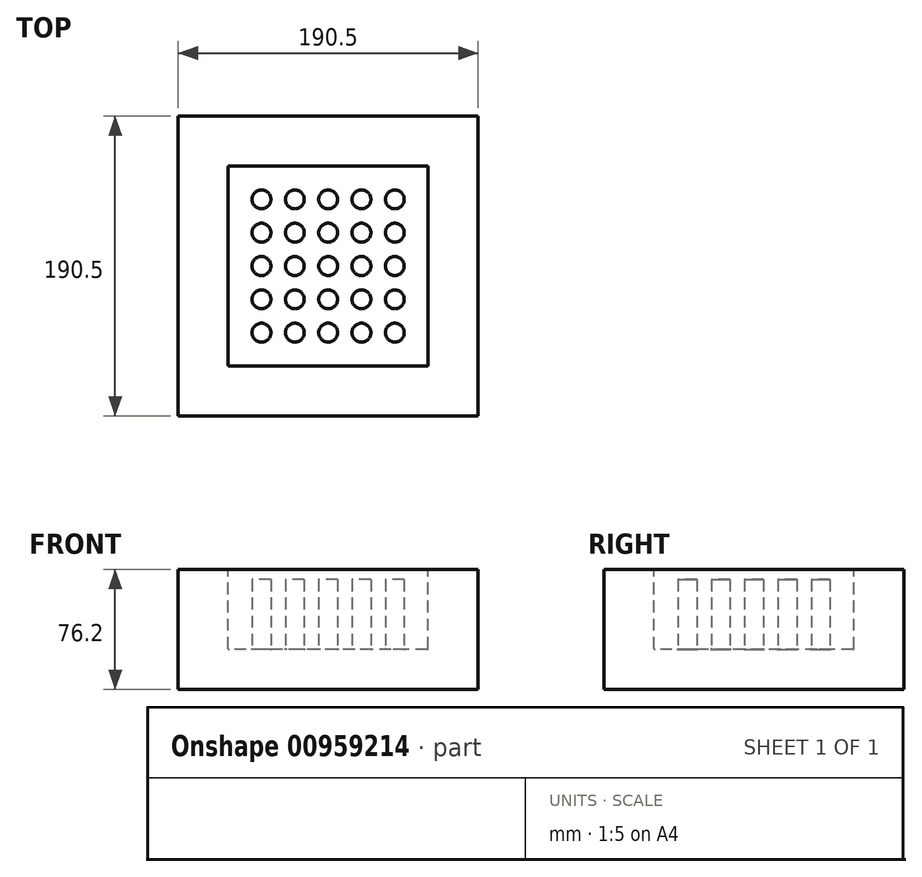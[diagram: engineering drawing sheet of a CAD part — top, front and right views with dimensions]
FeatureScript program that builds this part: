
annotation { "Feature Type Name" : "Feature", "Feature Type Description" : "" }
export const myFeature = defineFeature(function(context is Context, id is Id, definition is map)
    precondition{}
    {
        {
            var Q0;
            Q0=qCreatedBy(makeId("Top.planeOp"),FACE);
            var sketch = newSketch(context, id + "F0", { "sketchPlane" : qUnion([Q0])});
            skLineSegment(sketch, "E0.bottom", {"start": v(95.25, 95.25) * mm, "end": v(-95.25, 95.25) * mm});
            skLineSegment(sketch, "E0.top", {"start": v(95.25, -95.25) * mm, "end": v(-95.25, -95.25) * mm});
            skLineSegment(sketch, "E0.left", {"start": v(95.25, 95.25) * mm, "end": v(95.25, -95.25) * mm});
            skLineSegment(sketch, "E0.right", {"start": v(-95.25, 95.25) * mm, "end": v(-95.25, -95.25) * mm});
            skPoint(sketch, "E0.middle", {"position": v(0, 0) * mm});
            skSolve(sketch);
        }
        {
            var Q0;
            Q0 = qSketchRegion(id + "F0", true);
            extrude(context, id + "F1", {"entities" : qUnion([Q0]), "depth" : 76.2 * mm, "offsetDistance" : 25.4 * mm});
        }
        {
            var Q0;
            Q0=makeQuery(id+"F1.opExtrude","CAP_FACE",FACE,{"disambiguationData":[OSD([sQuery(id+"F0.wireOp",EDGE,"E0.bottom"),sQuery(id+"F0.wireOp",EDGE,"E0.top"),sQuery(id+"F0.wireOp",EDGE,"E0.left"),sQuery(id+"F0.wireOp",EDGE,"E0.right")])],"isStart":false});
            var sketch = newSketch(context, id + "F2", { "sketchPlane" : qUnion([Q0])});
            skLineSegment(sketch, "E1.bottom", {"start": v(63.5, 63.5) * mm, "end": v(-63.5, 63.5) * mm});
            skLineSegment(sketch, "E1.top", {"start": v(63.5, -63.5) * mm, "end": v(-63.5, -63.5) * mm});
            skLineSegment(sketch, "E1.left", {"start": v(63.5, 63.5) * mm, "end": v(63.5, -63.5) * mm});
            skLineSegment(sketch, "E1.right", {"start": v(-63.5, 63.5) * mm, "end": v(-63.5, -63.5) * mm});
            skPoint(sketch, "E1.middle", {"position": v(0, 0) * mm});
            skSolve(sketch);
        }
        {
            var Q0;
            Q0 = qSketchRegion(id + "F2", true);
            extrude(context, id + "F3", {"entities" : qUnion([Q0]), "operationType" : NewBodyOperationType.REMOVE, "oppositeDirection" : true, "depth" : 50.8 * mm, "offsetDistance" : 25.4 * mm});
        }
        {
            var Q0;
            Q0=makeQuery(id+"F3.boolean.opBoolean","COPY",FACE,{"derivedFrom":makeQuery(id+"F3.opExtrude","CAP_FACE",FACE,{"disambiguationData":[OSD([sQuery(id+"F2.wireOp",EDGE,"E1.bottom"),sQuery(id+"F2.wireOp",EDGE,"E1.top"),sQuery(id+"F2.wireOp",EDGE,"E1.left"),sQuery(id+"F2.wireOp",EDGE,"E1.right")])],"isStart":false})});
            var sketch = newSketch(context, id + "F4", { "sketchPlane" : qUnion([Q0])});
            skLineSegment(sketch, "E2", {"start": v(-63.5, 63.5) * mm, "end": v(-63.5, -63.5) * mm, "construction": true});
            skLineSegment(sketch, "E3.1.0.0", {"start": v(-42.33, 63.5) * mm, "end": v(-42.33, -63.5) * mm, "construction": true});
            skLineSegment(sketch, "E3.2.0.0", {"start": v(-21.17, 63.5) * mm, "end": v(-21.17, -63.5) * mm, "construction": true});
            skLineSegment(sketch, "E3.3.0.0", {"start": v(0, 63.5) * mm, "end": v(0, -63.5) * mm, "construction": true});
            skLineSegment(sketch, "E3.4.0.0", {"start": v(21.17, 63.5) * mm, "end": v(21.17, -63.5) * mm, "construction": true});
            skLineSegment(sketch, "E3.5.0.0", {"start": v(42.33, 63.5) * mm, "end": v(42.33, -63.5) * mm, "construction": true});
            skLineSegment(sketch, "E3.direction1", {"start": v(-63.5, -63.5) * mm, "end": v(-42.33, -63.5) * mm, "construction": true});
            skLineSegment(sketch, "E4", {"start": v(-63.5, -63.5) * mm, "end": v(63.5, -63.5) * mm, "construction": true});
            skLineSegment(sketch, "E5.0.1.0", {"start": v(-63.5, -42.33) * mm, "end": v(63.5, -42.33) * mm, "construction": true});
            skLineSegment(sketch, "E5.0.2.0", {"start": v(-63.5, -21.17) * mm, "end": v(63.5, -21.17) * mm, "construction": true});
            skLineSegment(sketch, "E5.0.3.0", {"start": v(-63.5, 0) * mm, "end": v(63.5, 0) * mm, "construction": true});
            skLineSegment(sketch, "E5.0.4.0", {"start": v(-63.5, 21.17) * mm, "end": v(63.5, 21.17) * mm, "construction": true});
            skLineSegment(sketch, "E5.0.5.0", {"start": v(-63.5, 42.33) * mm, "end": v(63.5, 42.33) * mm, "construction": true});
            skLineSegment(sketch, "E5.direction1", {"start": v(-63.5, -63.5) * mm, "end": v(-38.5, -63.5) * mm, "construction": true});
            skLineSegment(sketch, "E5.direction2", {"start": v(-63.5, -63.5) * mm, "end": v(-63.5, -42.33) * mm, "construction": true});
            skCircle(sketch, "E6", {"center": v(-42.33, -42.33) * mm, "radius": 6 * mm});
            skCircle(sketch, "E7.0.1.0", {"center": v(-42.33, -21.17) * mm, "radius": 6 * mm});
            skCircle(sketch, "E7.0.2.0", {"center": v(-42.33, 0) * mm, "radius": 6 * mm});
            skCircle(sketch, "E7.0.3.0", {"center": v(-42.33, 21.17) * mm, "radius": 6 * mm});
            skCircle(sketch, "E7.0.4.0", {"center": v(-42.33, 42.33) * mm, "radius": 6 * mm});
            skCircle(sketch, "E7.1.0.0", {"center": v(-21.17, -42.33) * mm, "radius": 6 * mm});
            skCircle(sketch, "E7.1.1.0", {"center": v(-21.17, -21.17) * mm, "radius": 6 * mm});
            skCircle(sketch, "E7.1.2.0", {"center": v(-21.17, 0) * mm, "radius": 6 * mm});
            skCircle(sketch, "E7.1.3.0", {"center": v(-21.17, 21.17) * mm, "radius": 6 * mm});
            skCircle(sketch, "E7.1.4.0", {"center": v(-21.17, 42.33) * mm, "radius": 6 * mm});
            skCircle(sketch, "E7.2.0.0", {"center": v(0, -42.33) * mm, "radius": 6 * mm});
            skCircle(sketch, "E7.2.1.0", {"center": v(0, -21.17) * mm, "radius": 6 * mm});
            skCircle(sketch, "E7.2.2.0", {"center": v(0, 0) * mm, "radius": 6 * mm});
            skCircle(sketch, "E7.2.3.0", {"center": v(0, 21.17) * mm, "radius": 6 * mm});
            skCircle(sketch, "E7.2.4.0", {"center": v(0, 42.33) * mm, "radius": 6 * mm});
            skCircle(sketch, "E7.3.0.0", {"center": v(21.17, -42.33) * mm, "radius": 6 * mm});
            skCircle(sketch, "E7.3.1.0", {"center": v(21.17, -21.17) * mm, "radius": 6 * mm});
            skCircle(sketch, "E7.3.2.0", {"center": v(21.17, 0) * mm, "radius": 6 * mm});
            skCircle(sketch, "E7.3.3.0", {"center": v(21.17, 21.17) * mm, "radius": 6 * mm});
            skCircle(sketch, "E7.3.4.0", {"center": v(21.17, 42.33) * mm, "radius": 6 * mm});
            skCircle(sketch, "E7.4.0.0", {"center": v(42.33, -42.33) * mm, "radius": 6 * mm});
            skCircle(sketch, "E7.4.1.0", {"center": v(42.33, -21.17) * mm, "radius": 6 * mm});
            skCircle(sketch, "E7.4.2.0", {"center": v(42.33, 0) * mm, "radius": 6 * mm});
            skCircle(sketch, "E7.4.3.0", {"center": v(42.33, 21.17) * mm, "radius": 6 * mm});
            skCircle(sketch, "E7.4.4.0", {"center": v(42.33, 42.33) * mm, "radius": 6 * mm});
            skLineSegment(sketch, "E7.direction1", {"start": v(-42.33, -42.33) * mm, "end": v(-21.17, -42.33) * mm, "construction": true});
            skLineSegment(sketch, "E7.direction2", {"start": v(-42.33, -42.33) * mm, "end": v(-42.33, -21.17) * mm, "construction": true});
            skSolve(sketch);
        }
        {
            var Q0;
            Q0 = qSketchRegion(id + "F4", true);
            extrude(context, id + "F5", {"entities" : qUnion([Q0]), "operationType" : NewBodyOperationType.ADD, "depth" : 44.45 * mm, "offsetDistance" : 25 * mm});
        }
        {
            var Q0;
            Q0=makeQuery(id+"F3.boolean.opBoolean","COPY",FACE,{"derivedFrom":makeQuery(id+"F3.opExtrude","CAP_FACE",FACE,{"disambiguationData":[OSD([sQuery(id+"F2.wireOp",EDGE,"E1.bottom"),sQuery(id+"F2.wireOp",EDGE,"E1.top"),sQuery(id+"F2.wireOp",EDGE,"E1.left"),sQuery(id+"F2.wireOp",EDGE,"E1.right")])],"isStart":false})});
            var Q1;
            Q1=makeQuery(id+"F3.boolean.opBoolean","COPY",EDGE,{"derivedFrom":makeQuery(id+"F3.opExtrude","SWEPT_EDGE",EDGE,{"disambiguationData":[OSD([sQuery(id+"F2.wireOp",EDGE,"E1.bottom"),sQuery(id+"F2.wireOp",EDGE,"E1.left")])]})});
            var Q2;
            Q2=makeQuery(id+"F3.boolean.opBoolean","COPY",EDGE,{"derivedFrom":makeQuery(id+"F3.opExtrude","SWEPT_EDGE",EDGE,{"disambiguationData":[OSD([sQuery(id+"F2.wireOp",EDGE,"E1.bottom"),sQuery(id+"F2.wireOp",EDGE,"E1.right")])]})});
            var Q3;
            Q3=makeQuery(id+"F3.boolean.opBoolean","COPY",EDGE,{"derivedFrom":makeQuery(id+"F3.opExtrude","SWEPT_EDGE",EDGE,{"disambiguationData":[OSD([sQuery(id+"F2.wireOp",EDGE,"E1.top"),sQuery(id+"F2.wireOp",EDGE,"E1.right")])]})});
            var Q4;
            Q4=makeQuery(id+"F3.boolean.opBoolean","COPY",EDGE,{"derivedFrom":makeQuery(id+"F3.opExtrude","SWEPT_EDGE",EDGE,{"disambiguationData":[OSD([sQuery(id+"F2.wireOp",EDGE,"E1.top"),sQuery(id+"F2.wireOp",EDGE,"E1.left")])]})});
            fillet(context, id + "F6", {"entities" : qUnion([Q0, Q1, Q2, Q3, Q4]), "radius" : 0.5 * mm, "tangentPropagation" : true, "allowEdgeOverflow" : false});
        }
    });
